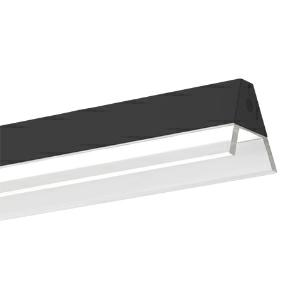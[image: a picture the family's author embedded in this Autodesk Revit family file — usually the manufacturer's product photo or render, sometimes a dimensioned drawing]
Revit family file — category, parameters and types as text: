
# Revit family: 3f_filippi_-_3f_mirella_di_sp_3f_filippi_-_10902_-_3f_mirella_bk_di_40_8_sp_l1480_ed3a
name_source: partatom
category: Lighting Fixtures
units: mm (PartAtom-declared; Revit-internal decimal feet)

## family parameters
Cut with Voids When Loaded = No
Host = Face
Light Source = No
Part Type = Normal
Room Calculation Point = No
Round Connector Dimension = Use Diameter
Shared = No

## types (1)
- 3F Filippi - 3F Mirella DI SP (1 x LED, 5849 lm, 58 W, 4000 K)
    Apparent Load = 58 VA
    Approval mark = ENEC
    CIE Flux Codes = 62 95 99 79 100
    Color Rendering = 80
    Color Temperature = 4000 K
    Control Gear = Electronic ballast
    Default Elevation = 1800 mm
    Description = ILLUMINOTECHNICAL
Luminous efficiency 100% (DLOR 79%, ULOR 21%).
Initial luminous flux of the luminaire 5849 lm.
Symmetric direct-indirect distribution.
Installation Interdistance Transv.D = 1.65 x hu - Long.D = 1.26 x hu.
Average luminance <3000 cd/m² for radial angles >65°.
Tabular UGR (CIE 117 - 4H-8H; S=0.25H; 70/50/20): RUG 16.3 - 17.4.
Beam angle: 89° - 96°.
Luminous efficacy 101 lm/W.
Lifetime (L93/B10): 30000 h. (tq+25°C)
Lifetime (L90/B10): 50000 h. (tq+25°C)
Lifetime (L85/B10): 80000 h. (tq+25°C)
Lifetime (L80/B10): 100000 h. (tq+25°C)
Sudden decreased luminous flux after 50000 hours: 0% (C0).
Photobiological safety in compliance with IEC/TR 62778: RG0 risk exempt, (IEC 62471).
In compliance with IEC/EN 62722-2-1 - IEC/EN 62717 standards.

SOURCE
One 40W/840 linear LED module for direct lighting + one 8W/840 linear LED module for indirect lighting.
Energy efficiency class (UE 2019/2020 - UE 2019/2015): D, E.
CIE 13.3 Colour rendering index: CRI >80 (R9 <50%).
IES TM-30 Fidelity Index: Rf = 84 Rg = 95.
CCT nominal colour temperature 4000 K.
Colour initial tolerance (MacAdam): SDCM 3.

MECHANICAL
Extruded aluminium housing, painted in black.
Methacrylate (PMMA) primary lens for total source shielding.
Highly aesthetic external lens in transparent methacrylate (PMMA) for optimizing light distribution.
Flat transparent prismatic methacrylate (PMMA) filter, multi-lenticular exterior, anti-glare.
Upper film in translucent polycarbonate, self-extinguishing, UV stabilised.
Black painted aluminium end caps.
Luminaire with limited surface temperature. - D - (EN 60598-2-24)
Dimensions: 1480x112 mm, height 91 mm. Weight 5.9 kg.
IP40 protection degree.
Mechanical strength to impacts IK06 (1 joule).
Glow-wire test resistance 650°C.

ELECTRICAL
Halogen Free electronic wiring 230V-50/60Hz, power factor 0.95, THD <25%, constant output current, SELV, class I, 2 driver.
Power of the luminaire 58 W.
CE - IEC 60598-1 - EN 60598-1.
SAFE FLICKER: PstLM=<1 and SVM=<0.4 (IEC TR 61547-1 and IEC TR 63158), to ensure a more comfortable and safe light.
Luminaire compliant with EN 60598-2-22 for power supply from a centralised emergency system CPSS (Central Power Supply System), not incorporated in the luminaire - high risk areas excluded. The default power and flux are 100% in AC and 100% in DC.
Ambient temperature from 0°C to +25°C.
Temperature class T6 max 85°C.
Relative humidity UR: <85%.

INSTALLATION
Suspended.

SUPPLIED
Suspensions with chrome bosses and quick adjusters, 2 m galvanised steel cable.
Transparent 2.3 m 3x0.75 mm² power cable with white power supply case for mounting on the ceiling.

APPLICATIONS
Environments involving accurate visual tasks where a diffused and soft light for an optimum visual comfort and the source total shielding are required.
In environments with VDTs, managerial offices and staterooms.

WARNING
Luminaire designed for disposal/recycling at end-of-life.
Replaceable (LED only) light source by a professional. Replaceable control gear by a professional.
    Height = 91 mm
    Lamp = 1 x LED
    Lamp Light Flux = 5849 lm
    Lamp Power = 58 W
    Lamp count = 1
    Length = 1480 mm
    Lifetime = 50000 h
    Luminous efficacy = 101 lm/W
    Manufacturer = 3F Filippi
    ModVariant = No
    Model = 3F Filippi - 10902 - 3F Mirella BK DI 40+8 SP L1480
    Mounting Place = Ceiling
    Mounting Type = Pendant
    Number of Poles = 1
    OnlyDefault = Yes
    Power Factor = 1
    Product Name = 3F Filippi - 3F Mirella DI SP
    Product group = pendant luminaire
    ProductGroupID = 9
    Protection Class = Protection class I
    Protection Degree = IP 40
    RLX_Detail_Level = 1
    RLX_Emergency_Light_Flux = 0 lm
    RLX_Emergency_Type = 0
    RLX_Emergency_Type_DB = No
    RlxData = <blob elided: 66173 chars, md5=ca7abbf0>
    Socket = socket
    Standby Power = 0 W
    System Light Flux = 5849 lm
    System Power = 58 W
    Type Comments = Product without accessories
    Type Image = 3ffilippi_3f_mirella_bk.jpg
    URL = http://relux.com
    VarID = ---
    Voltage = 0 V
    Weight = 0.00 kg
    Width = 112 mm

## geometry (parser evidence)
native form markers: Blend x4, Sweep x13
no freeform markers — native parametric forms only
